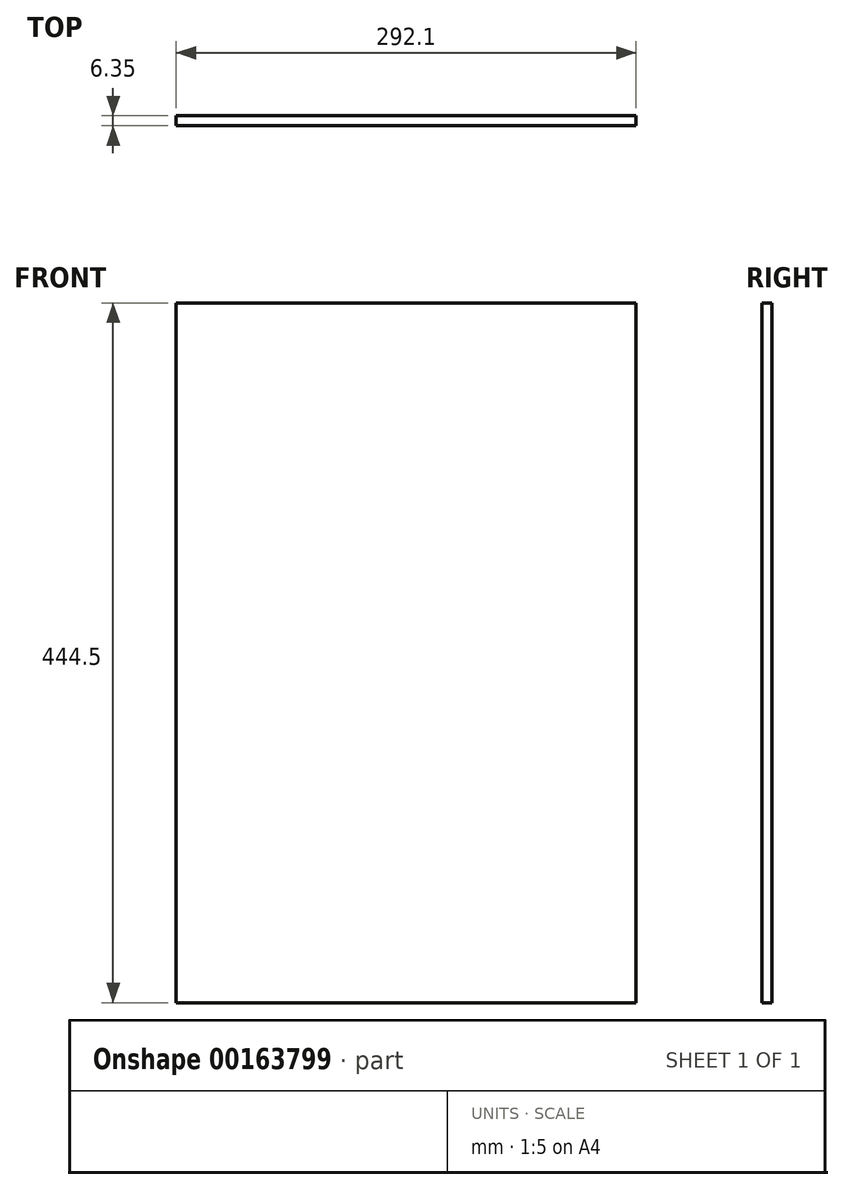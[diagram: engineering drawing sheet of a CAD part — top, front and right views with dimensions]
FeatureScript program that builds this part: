
annotation { "Feature Type Name" : "Feature", "Feature Type Description" : "" }
export const myFeature = defineFeature(function(context is Context, id is Id, definition is map)
    precondition{}
    {
        {
            var Q0;
            Q0=qCreatedBy(makeId("Front.planeOp"),FACE);
            var sketch = newSketch(context, id + "F0", { "sketchPlane" : qUnion([Q0])});
            skLineSegment(sketch, "E0.bottom", {"start": v(-146.05, -222.25) * mm, "end": v(146.05, -222.25) * mm});
            skLineSegment(sketch, "E0.top", {"start": v(-146.05, 222.25) * mm, "end": v(146.05, 222.25) * mm});
            skLineSegment(sketch, "E0.left", {"start": v(-146.05, -222.25) * mm, "end": v(-146.05, 222.25) * mm});
            skLineSegment(sketch, "E0.right", {"start": v(146.05, -222.25) * mm, "end": v(146.05, 222.25) * mm});
            skPoint(sketch, "E0.middle", {"position": v(0, 0) * mm});
            skSolve(sketch);
        }
        {
            var Q0;
            Q0=qSketchRegion(id+"F0",true);
            extrude(context, id + "F1", {"entities" : qUnion([Q0]), "depth" : 6.35 * mm});
        }
    });
